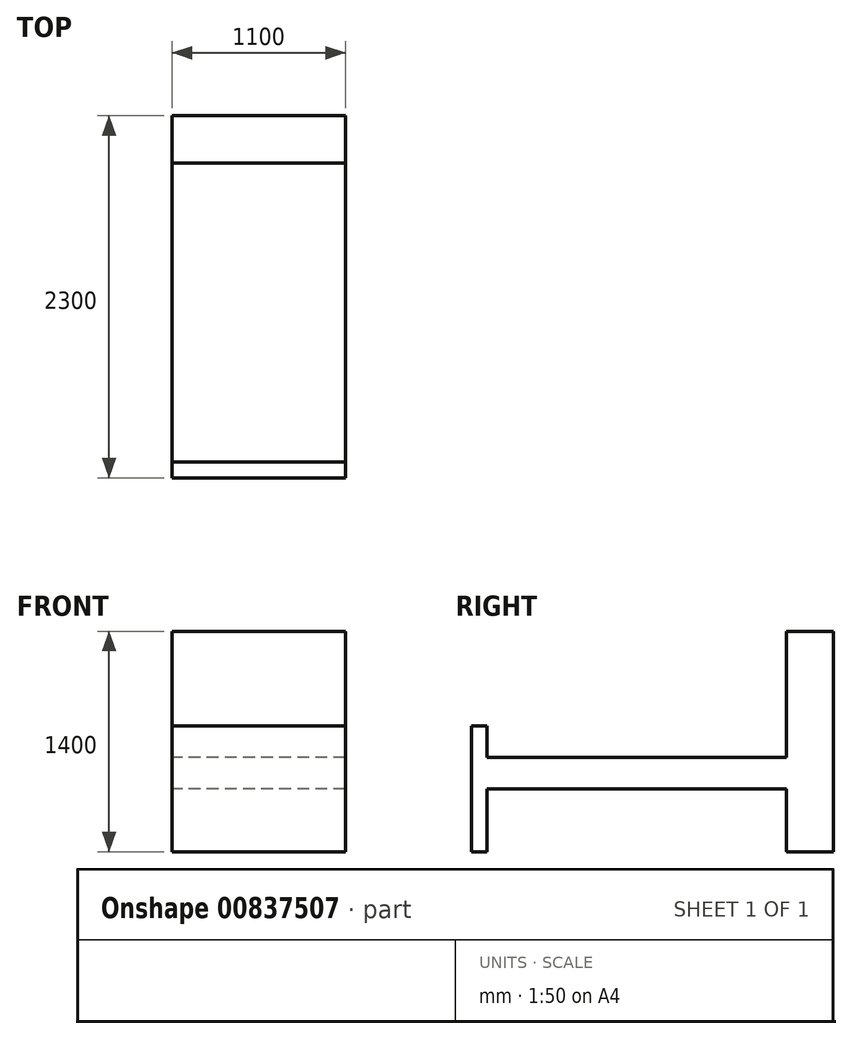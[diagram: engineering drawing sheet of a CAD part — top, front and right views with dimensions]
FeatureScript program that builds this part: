
annotation { "Feature Type Name" : "Feature", "Feature Type Description" : "" }
export const myFeature = defineFeature(function(context is Context, id is Id, definition is map)
    precondition{}
    {
        {
            var Q0;
            Q0=qCreatedBy(makeId("Right.planeOp"),FACE);
            var sketch = newSketch(context, id + "F0", { "sketchPlane" : qUnion([Q0])});
            skLineSegment(sketch, "E0.bottom", {"start": v(0, 0) * mm, "end": v(-300, 0) * mm});
            skLineSegment(sketch, "E0.top", {"start": v(0, 1400) * mm, "end": v(-300, 1400) * mm});
            skLineSegment(sketch, "E0.left", {"start": v(0, 0) * mm, "end": v(0, 1400) * mm});
            skLineSegment(sketch, "E0.right", {"start": v(-300, 0) * mm, "end": v(-300, 1400) * mm});
            skLineSegment(sketch, "E1.bottom", {"start": v(-300, 400) * mm, "end": v(-2200, 400) * mm});
            skLineSegment(sketch, "E1.top", {"start": v(-300, 600) * mm, "end": v(-2200, 600) * mm});
            skLineSegment(sketch, "E1.left", {"start": v(-300, 400) * mm, "end": v(-300, 600) * mm});
            skLineSegment(sketch, "E1.right", {"start": v(-2200, 400) * mm, "end": v(-2200, 600) * mm});
            skLineSegment(sketch, "E2.bottom", {"start": v(-2300, 800) * mm, "end": v(-2200, 800) * mm});
            skLineSegment(sketch, "E2.top", {"start": v(-2300, 0) * mm, "end": v(-2200, 0) * mm});
            skLineSegment(sketch, "E2.left", {"start": v(-2300, 800) * mm, "end": v(-2300, 0) * mm});
            skLineSegment(sketch, "E2.right", {"start": v(-2200, 800) * mm, "end": v(-2200, 0) * mm});
            skSolve(sketch);
        }
        {
            var Q0;
            {var subQ1=sQuery(id+"F0.wireOp",EDGE,"E0.bottom");Q0=makeQuery(id+"F0.imprint","IMPRINT",FACE,{"disambiguationData":[TD([[makeQuery(id+"F0.imprint","IMPRINT",EDGE,{"derivedFrom":subQ1}),-1.0]])]});}
            var Q1;
            {var subQ0=sQuery(id+"F0.wireOp",EDGE,"E1.bottom");Q1=makeQuery(id+"F0.imprint","IMPRINT",FACE,{"disambiguationData":[TD([[makeQuery(id+"F0.imprint","IMPRINT",EDGE,{"derivedFrom":subQ0}),-1.0]])]});}
            var Q2;
            {var subQ2=sQuery(id+"F0.wireOp",EDGE,"E2.bottom");Q2=makeQuery(id+"F0.imprint","IMPRINT",FACE,{"disambiguationData":[TD([[makeQuery(id+"F0.imprint","IMPRINT",EDGE,{"derivedFrom":subQ2}),-1.0]])]});}
            extrude(context, id + "F1", {"entities" : qUnion([Q0, Q1, Q2]), "depth" : 1100 * mm, "offsetDistance" : 25 * mm, "symmetric" : true});
        }
    });
